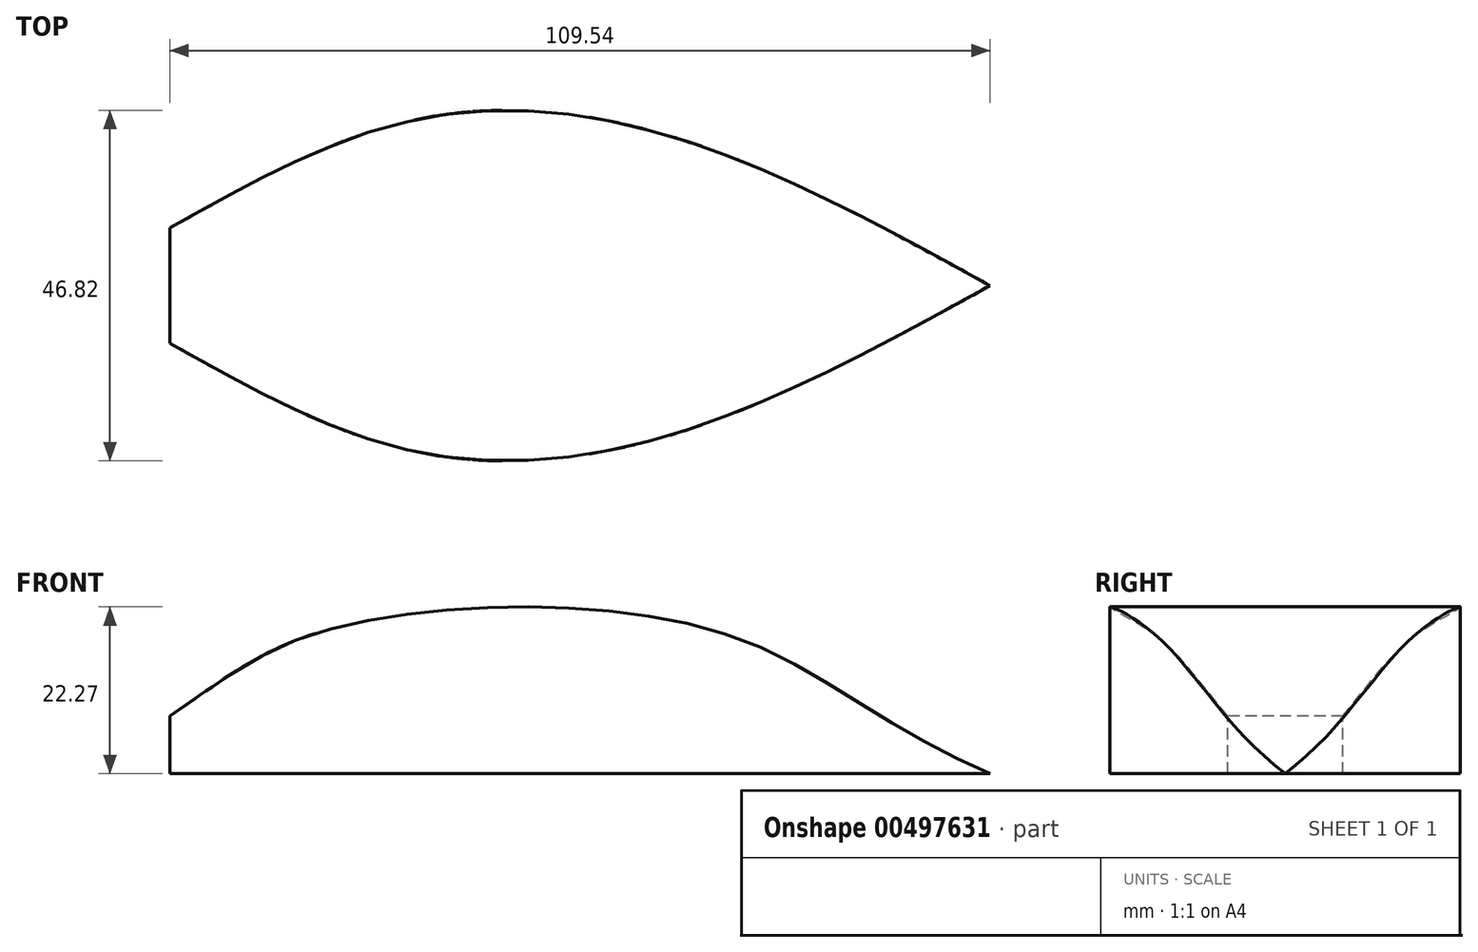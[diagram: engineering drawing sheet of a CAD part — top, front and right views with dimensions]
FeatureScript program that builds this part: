
annotation { "Feature Type Name" : "Feature", "Feature Type Description" : "" }
export const myFeature = defineFeature(function(context is Context, id is Id, definition is map)
    precondition{}
    {
        {
            var Q0;
            Q0=qCreatedBy(makeId("Front.planeOp"),FACE);
            var sketch = newSketch(context, id + "F0", { "sketchPlane" : qUnion([Q0])});
            skLineSegment(sketch, "E0.bottom", {"start": v(0, 0) * mm, "end": v(109.54, 0) * mm});
            skLineSegment(sketch, "E0.top", {"start": v(0, 28.13) * mm, "end": v(109.54, 28.13) * mm});
            skLineSegment(sketch, "E0.left", {"start": v(0, 0) * mm, "end": v(0, 28.13) * mm});
            skLineSegment(sketch, "E0.right", {"start": v(109.54, 0) * mm, "end": v(109.54, 28.13) * mm});
            skSolve(sketch);
        }
        {
            var Q0;
            Q0 = qSketchRegion(id + "F0", true);
            extrude(context, id + "F1", {"entities" : qUnion([Q0]), "depth" : 35 * mm, "hasSecondDirection" : true, "secondDirectionOppositeDirection" : true, "secondDirectionDepth" : 35 * mm});
        }
        {
            var Q0;
            Q0=makeQuery(id+"F1.opExtrude","SWEPT_FACE",FACE,{"disambiguationData":[OSD([sQuery(id+"F0.wireOp",EDGE,"E0.right")])]});
            var sketch = newSketch(context, id + "F2", { "sketchPlane" : qUnion([Q0])});
            skPoint(sketch, "E1.1.internal.snap0", {"position": v(0, 0) * mm});
            skLineSegment(sketch, "E2", {"start": v(-35, 0) * mm, "end": v(35, 0) * mm});
            skFitSpline(sketch, "E3", {"points": [v(-22.5, 0) * mm, v(0, 12.43) * mm, v(11.25, 10.95) * mm], "startDerivative": vector(40.23, 28.03) * mm, "endDerivative": vector(26.33, -8.58) * mm});
            skLineSegment(sketch, "E4", {"start": v(0, 12.43) * mm, "end": v(0, 0) * mm});
            skFitSpline(sketch, "E5.MirrorCS", {"points": [v(22.5, 0) * mm, v(0, 12.43) * mm, v(-11.25, 10.95) * mm], "startDerivative": vector(-40.23, 28.03) * mm, "endDerivative": vector(-26.33, -8.58) * mm});
            skSolve(sketch);
        }
        {
            var Q0;
            Q0=makeQuery(id+"F1.opExtrude","SWEPT_FACE",FACE,{"disambiguationData":[OSD([sQuery(id+"F0.wireOp",EDGE,"E0.top")])]});
            var sketch = newSketch(context, id + "F3", { "sketchPlane" : qUnion([Q0])});
            skFitSpline(sketch, "E6", {"points": [v(0, 7.7) * mm, v(32.96, 22.2) * mm, v(68.2, 19.54) * mm, v(109.54, 0) * mm], "startDerivative": vector(100.8, 56.67) * mm, "endDerivative": vector(114.8, -63.19) * mm});
            skLineSegment(sketch, "E7", {"start": v(109.54, 0) * mm, "end": v(0, 0) * mm});
            skLineSegment(sketch, "E8", {"start": v(0, 0) * mm, "end": v(0, 7.7) * mm});
            skFitSpline(sketch, "E9.MirrorCS", {"points": [v(0, -7.7) * mm, v(32.96, -22.2) * mm, v(68.2, -19.54) * mm, v(109.54, 0) * mm], "startDerivative": vector(100.8, -56.67) * mm, "endDerivative": vector(114.8, 63.19) * mm});
            skLineSegment(sketch, "E10.MirrorCS", {"start": v(0, 0) * mm, "end": v(0, -7.7) * mm});
            skSolve(sketch);
        }
        {
            var Q0;
            Q0=makeQuery(id+"F1.opExtrude","CAP_FACE",FACE,{"disambiguationData":[OSD([sQuery(id+"F0.wireOp",EDGE,"E0.bottom"),sQuery(id+"F0.wireOp",EDGE,"E0.top"),sQuery(id+"F0.wireOp",EDGE,"E0.left"),sQuery(id+"F0.wireOp",EDGE,"E0.right")])],"isStart":false});
            var sketch = newSketch(context, id + "F4", { "sketchPlane" : qUnion([Q0])});
            skFitSpline(sketch, "E11", {"points": [v(0, 7.7) * mm, v(21.12, 19.24) * mm, v(73.22, 18.95) * mm, v(109.54, 0) * mm], "startDerivative": vector(84.96, 57.01) * mm, "endDerivative": vector(133.13, -55.17) * mm});
            skLineSegment(sketch, "E12", {"start": v(0, 7.7) * mm, "end": v(0, 0) * mm});
            skLineSegment(sketch, "E13", {"start": v(0, 0) * mm, "end": v(109.54, 0) * mm});
            skSolve(sketch);
        }
        {
            var Q0;
            Q0 = qSketchRegion(id + "F3", true);
            extrude(context, id + "F5", {"entities" : qUnion([Q0]), "operationType" : NewBodyOperationType.INTERSECT, "oppositeDirection" : true, "depth" : 31 * mm});
        }
        {
            var Q0;
            Q0 = qSketchRegion(id + "F4", true);
            extrude(context, id + "F6", {"entities" : qUnion([Q0]), "operationType" : NewBodyOperationType.INTERSECT, "oppositeDirection" : true, "depth" : 100 * mm});
        }
    });
